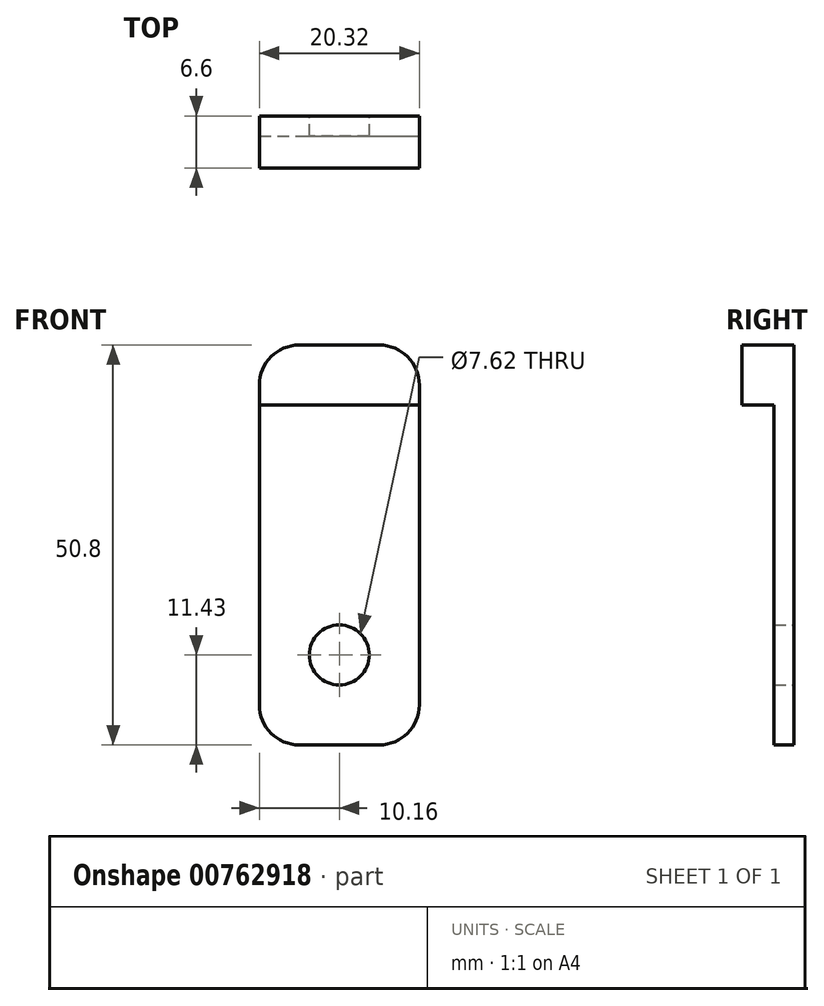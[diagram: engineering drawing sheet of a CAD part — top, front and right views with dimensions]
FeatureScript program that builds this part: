
annotation { "Feature Type Name" : "Feature", "Feature Type Description" : "" }
export const myFeature = defineFeature(function(context is Context, id is Id, definition is map)
    precondition{}
    {
        {
            var Q0;
            Q0=qCreatedBy(makeId("Front.planeOp"),FACE);
            var sketch = newSketch(context, id + "F0", { "sketchPlane" : qUnion([Q0])});
            skCircle(sketch, "E0", {"center": v(0, 0) * mm, "radius": 3.81 * mm});
            skLineSegment(sketch, "E1.bottom", {"start": v(-5.08, -11.43) * mm, "end": v(5.08, -11.43) * mm});
            skLineSegment(sketch, "E1.top", {"start": v(-5.08, 39.37) * mm, "end": v(5.08, 39.37) * mm});
            skLineSegment(sketch, "E1.left", {"start": v(-10.16, -6.35) * mm, "end": v(-10.16, 34.3) * mm});
            skLineSegment(sketch, "E1.right", {"start": v(10.16, -6.35) * mm, "end": v(10.16, 34.29) * mm});
            skPoint(sketch, "E2.end.orphan", {"position": v(10.16, -1.27) * mm});
            skPoint(sketch, "E2.start.orphan", {"position": v(3.81, 0) * mm});
            skPoint(sketch, "E3.end.orphan", {"position": v(0, -11.43) * mm});
            skPoint(sketch, "E3.start.orphan", {"position": v(0, -3.81) * mm});
            skPoint(sketch, "E4.end.orphan", {"position": v(-10.16, 0) * mm});
            skPoint(sketch, "E4.start.orphan", {"position": v(-3.81, 0) * mm});
            skLineSegment(sketch, "E5", {"start": v(-10.16, 34.29) * mm, "end": v(-10.16, 31.75) * mm});
            skLineSegment(sketch, "E6", {"start": v(-10.16, 31.75) * mm, "end": v(10.16, 31.75) * mm});
            skPoint(sketch, "E7.visualSharp", {"position": v(-10.16, 39.37) * mm});
            skArc(sketch, "E7.filletArc", {"start": v(-5.08, 39.37) * mm, "mid": v(-8.67, 37.88) * mm, "end": v(-10.16, 34.29) * mm});
            skPoint(sketch, "E8.visualSharp", {"position": v(10.16, 39.37) * mm});
            skArc(sketch, "E8.filletArc", {"start": v(10.16, 34.29) * mm, "mid": v(8.67, 37.88) * mm, "end": v(5.08, 39.37) * mm});
            skPoint(sketch, "E9.visualSharp", {"position": v(-10.16, -11.43) * mm});
            skArc(sketch, "E9.filletArc", {"start": v(-10.16, -6.35) * mm, "mid": v(-8.67, -9.94) * mm, "end": v(-5.08, -11.43) * mm});
            skPoint(sketch, "E10.visualSharp", {"position": v(10.16, -11.43) * mm});
            skArc(sketch, "E10.filletArc", {"start": v(5.08, -11.43) * mm, "mid": v(8.67, -9.94) * mm, "end": v(10.16, -6.35) * mm});
            skSolve(sketch);
        }
        {
            var Q0;
            Q0=makeQuery(id+"F0.imprint","IMPRINT",FACE,{"disambiguationData":[TD([[makeQuery(id+"F0.imprint","IMPRINT",EDGE,{"derivedFrom":sQuery(id+"F0.wireOp",EDGE,"E0")}),-1.0]])]});
            extrude(context, id + "F1", {"entities" : qUnion([Q0]), "depth" : 2.54 * mm, "offsetDistance" : 25.4 * mm});
        }
        {
            var Q0;
            Q0=makeQuery(id+"F0.imprint","IMPRINT",FACE,{"disambiguationData":[TD([[makeQuery(id+"F0.imprint","IMPRINT",EDGE,{"derivedFrom":sQuery(id+"F0.wireOp",EDGE,"E1.top")}),-1.0]])]});
            extrude(context, id + "F2", {"entities" : qUnion([Q0]), "operationType" : NewBodyOperationType.ADD, "depth" : 6.6 * mm, "offsetDistance" : 25.4 * mm});
        }
    });
